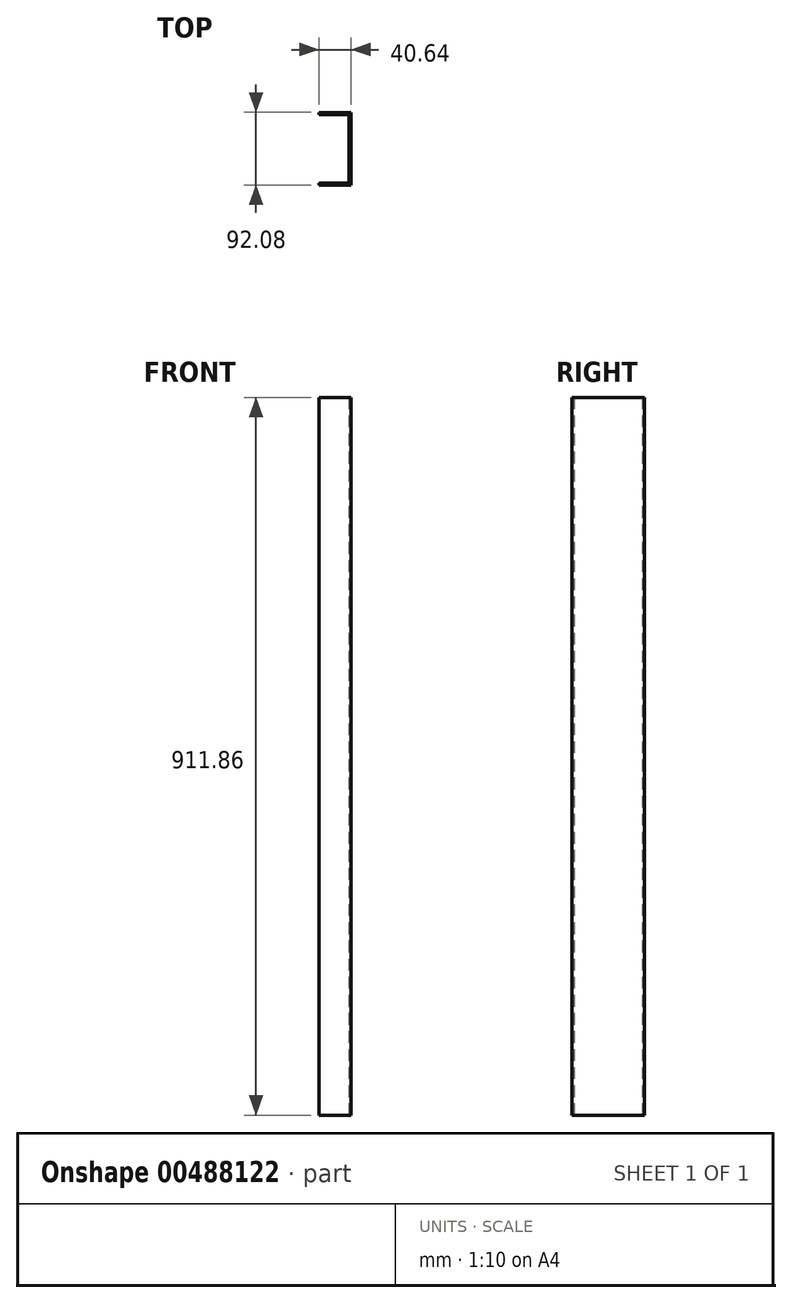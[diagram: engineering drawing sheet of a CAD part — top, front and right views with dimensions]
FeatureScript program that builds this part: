
annotation { "Feature Type Name" : "Feature", "Feature Type Description" : "" }
export const myFeature = defineFeature(function(context is Context, id is Id, definition is map)
    precondition{}
    {
        {
            var Q0;
            Q0=qCreatedBy(makeId("Top.planeOp"),FACE);
            var sketch = newSketch(context, id + "F0", { "sketchPlane" : qUnion([Q0])});
            skLineSegment(sketch, "E0", {"start": v(-38.1, 20.64) * mm, "end": v(0, 20.64) * mm});
            skLineSegment(sketch, "E1", {"start": v(0, 20.64) * mm, "end": v(0, -66.36) * mm});
            skLineSegment(sketch, "E2", {"start": v(0, -66.36) * mm, "end": v(-38.1, -66.36) * mm});
            skLineSegment(sketch, "E3.0", {"start": v(2.54, -68.9) * mm, "end": v(-38.1, -68.9) * mm});
            skLineSegment(sketch, "E3.1", {"start": v(2.54, 23.18) * mm, "end": v(2.54, -68.9) * mm});
            skLineSegment(sketch, "E3.2", {"start": v(-38.1, 23.18) * mm, "end": v(2.54, 23.18) * mm});
            skLineSegment(sketch, "E4", {"start": v(-38.1, -68.9) * mm, "end": v(-38.1, -66.36) * mm});
            skLineSegment(sketch, "E5", {"start": v(-38.1, 23.18) * mm, "end": v(-38.1, 20.64) * mm});
            skSolve(sketch);
        }
        {
            var Q0;
            Q0=makeQuery(id+"F0.imprint","IMPRINT",FACE,{"disambiguationData":[TD([[makeQuery(id+"F0.imprint","IMPRINT",EDGE,{"derivedFrom":sQuery(id+"F0.wireOp",EDGE,"E0")}),1.0]])]});
            extrude(context, id + "F1", {"entities" : qUnion([Q0]), "depth" : 911.86 * mm});
        }
    });
